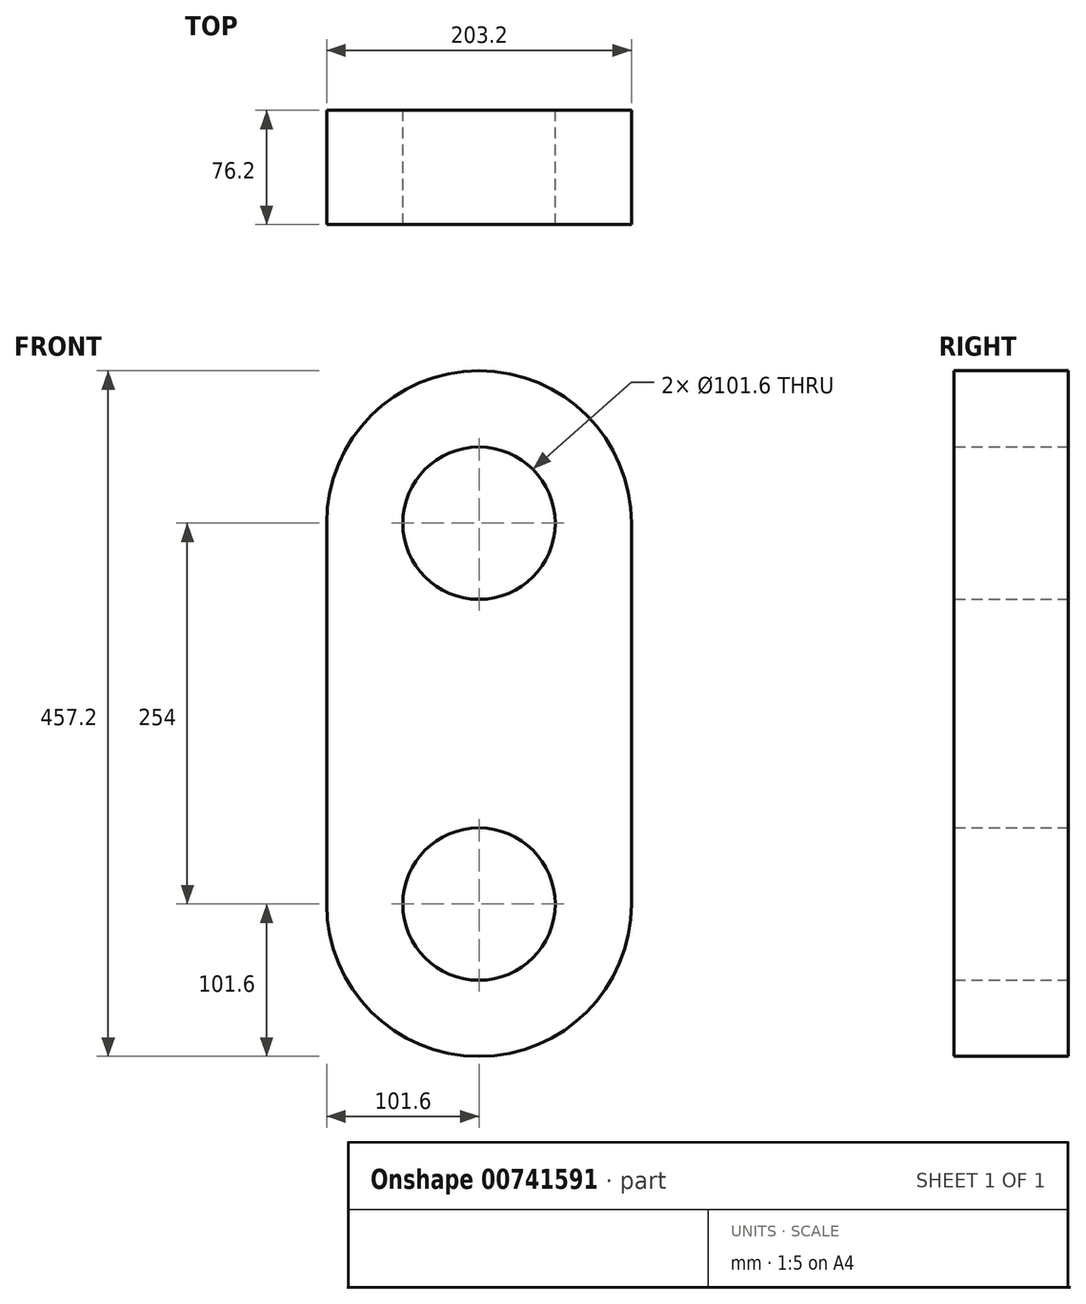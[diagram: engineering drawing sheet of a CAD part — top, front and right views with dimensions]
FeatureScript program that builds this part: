
annotation { "Feature Type Name" : "Feature", "Feature Type Description" : "" }
export const myFeature = defineFeature(function(context is Context, id is Id, definition is map)
    precondition{}
    {
        {
            var Q0;
            Q0=qCreatedBy(makeId("Front.planeOp"),FACE);
            var sketch = newSketch(context, id + "F0", { "sketchPlane" : qUnion([Q0])});
            skLineSegment(sketch, "E0.bottom", {"start": v(0, -101.6) * mm, "end": v(0, -101.6) * mm});
            skLineSegment(sketch, "E0.top", {"start": v(0, 355.6) * mm, "end": v(0, 355.6) * mm});
            skLineSegment(sketch, "E0.left", {"start": v(-101.6, 0) * mm, "end": v(-101.6, 254) * mm});
            skLineSegment(sketch, "E0.right", {"start": v(101.6, 0) * mm, "end": v(101.6, 254) * mm});
            skPoint(sketch, "E1.visualSharp", {"position": v(-101.6, 355.6) * mm});
            skArc(sketch, "E1.filletArc", {"start": v(0, 355.6) * mm, "mid": v(-71.84, 325.84) * mm, "end": v(-101.6, 254) * mm});
            skPoint(sketch, "E2.visualSharp", {"position": v(-101.6, -101.6) * mm});
            skArc(sketch, "E2.filletArc", {"start": v(-101.6, 0) * mm, "mid": v(-71.84, -71.84) * mm, "end": v(0, -101.6) * mm});
            skPoint(sketch, "E3.visualSharp", {"position": v(101.6, -101.6) * mm});
            skArc(sketch, "E3.filletArc", {"start": v(0, -101.6) * mm, "mid": v(71.84, -71.84) * mm, "end": v(101.6, 0) * mm});
            skPoint(sketch, "E4.visualSharp", {"position": v(101.6, 355.6) * mm});
            skArc(sketch, "E4.filletArc", {"start": v(101.6, 254) * mm, "mid": v(71.84, 325.84) * mm, "end": v(0, 355.6) * mm});
            skCircle(sketch, "E5", {"center": v(0, 254) * mm, "radius": 50.8 * mm});
            skCircle(sketch, "E6", {"center": v(0, 0) * mm, "radius": 50.8 * mm});
            skSolve(sketch);
        }
        {
            var Q0;
            Q0 = qSketchRegion(id + "F0", true);
            extrude(context, id + "F1", {"entities" : qUnion([Q0]), "depth" : 76.2 * mm, "offsetDistance" : 25.4 * mm});
        }
    });
